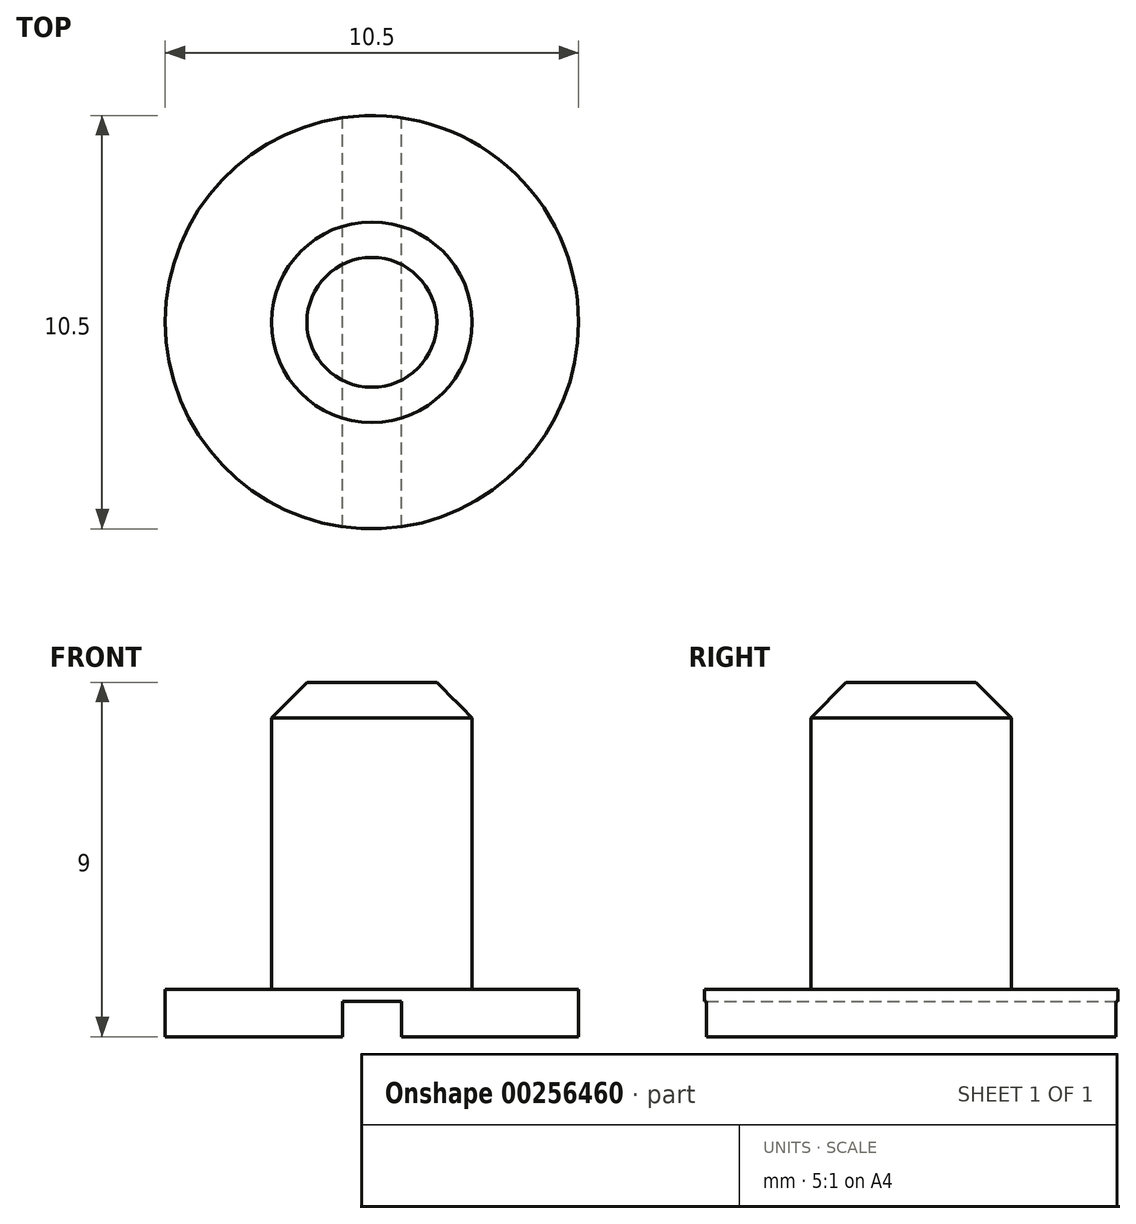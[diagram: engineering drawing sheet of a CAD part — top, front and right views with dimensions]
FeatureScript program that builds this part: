
annotation { "Feature Type Name" : "Feature", "Feature Type Description" : "" }
export const myFeature = defineFeature(function(context is Context, id is Id, definition is map)
    precondition{}
    {
        {
            var Q0;
            Q0=qCreatedBy(makeId("Top.planeOp"),FACE);
            var sketch = newSketch(context, id + "F0", { "sketchPlane" : qUnion([Q0])});
            skCircle(sketch, "E0", {"center": v(0, 0) * mm, "radius": 1.75 * mm});
            skSolve(sketch);
        }
        {
            var Q0;
            Q0=makeQuery(id+"F0.imprint","IMPRINT",FACE,{"disambiguationData":[TD([[makeQuery(id+"F0.imprint","IMPRINT",EDGE,{"derivedFrom":sQuery(id+"F0.wireOp",EDGE,"E0")}),1.0]])]});
            extrude(context, id + "F1", {"entities" : qUnion([Q0]), "depth" : 0.4 * mm});
        }
        {
            var Q0;
            Q0=makeQuery(id+"F1.opExtrude","CAP_FACE",FACE,{"disambiguationData":[OSD([sQuery(id+"F0.wireOp",EDGE,"E0")])],"isStart":false});
            var sketch = newSketch(context, id + "F2", { "sketchPlane" : qUnion([Q0])});
            skCircle(sketch, "E1", {"center": v(0, 0) * mm, "radius": 0.85 * mm});
            skSolve(sketch);
        }
        {
            var Q0;
            Q0=makeQuery(id+"F2.imprint","IMPRINT",FACE,{"disambiguationData":[TD([[makeQuery(id+"F2.imprint","IMPRINT",EDGE,{"derivedFrom":sQuery(id+"F2.wireOp",EDGE,"E1")}),1.0]])]});
            extrude(context, id + "F3", {"entities" : qUnion([Q0]), "operationType" : NewBodyOperationType.ADD, "depth" : 2.6 * mm});
        }
        {
            var Q0;
            Q0=makeQuery(id+"F1.opExtrude","CAP_FACE",FACE,{"disambiguationData":[OSD([sQuery(id+"F0.wireOp",EDGE,"E0")])],"isStart":true});
            var sketch = newSketch(context, id + "F4", { "sketchPlane" : qUnion([Q0])});
            skLineSegment(sketch, "E2", {"start": v(-0.25, 1.73) * mm, "end": v(-0.25, -1.73) * mm});
            skLineSegment(sketch, "E3", {"start": v(0.25, 1.73) * mm, "end": v(0.25, -1.73) * mm});
            skSolve(sketch);
        }
        {
            var Q0;
            {var subQ2=sQuery(id+"F4.wireOp",EDGE,"E2");Q0=makeQuery(id+"F4.imprint","IMPRINT",FACE,{"disambiguationData":[TD([[makeQuery(id+"F4.imprint","IMPRINT",EDGE,{"derivedFrom":subQ2}),1.0]])]});}
            extrude(context, id + "F5", {"entities" : qUnion([Q0]), "operationType" : NewBodyOperationType.REMOVE, "oppositeDirection" : true, "depth" : 0.3 * mm});
        }
        {
            var Q0;
            Q0=makeQuery(id+"F3.opExtrude","CAP_EDGE",EDGE,{"disambiguationData":[OSD([sQuery(id+"F2.wireOp",EDGE,"E1")])],"isStart":false});
            chamfer(context, id + "F6", {"entities" : qUnion([Q0]), "chamferType" : ChamferType.OFFSET_ANGLE, "width" : 0.3 * mm, "oppositeDirection" : false, "angle" : 45 * degree, "tangentPropagation" : true});
        }
        {
            var Q0;
            Q0=makeQuery(id+"F1.opExtrude","SWEPT_BODY",BODY,{"disambiguationData":[OSD([sQuery(id+"F0.wireOp",EDGE,"E0")])]});
            var Q1;
            Q1=qCreatedBy(makeId("Origin.pointOp"),VERTEX);
            transform(context, id + "F7", {"entities" : qUnion([Q0]), "transformType" : TransformType.SCALE_UNIFORMLY, "scale" : 3, "makeCopy" : false, "scalePoint" : qUnion([Q1])});
        }
    });
